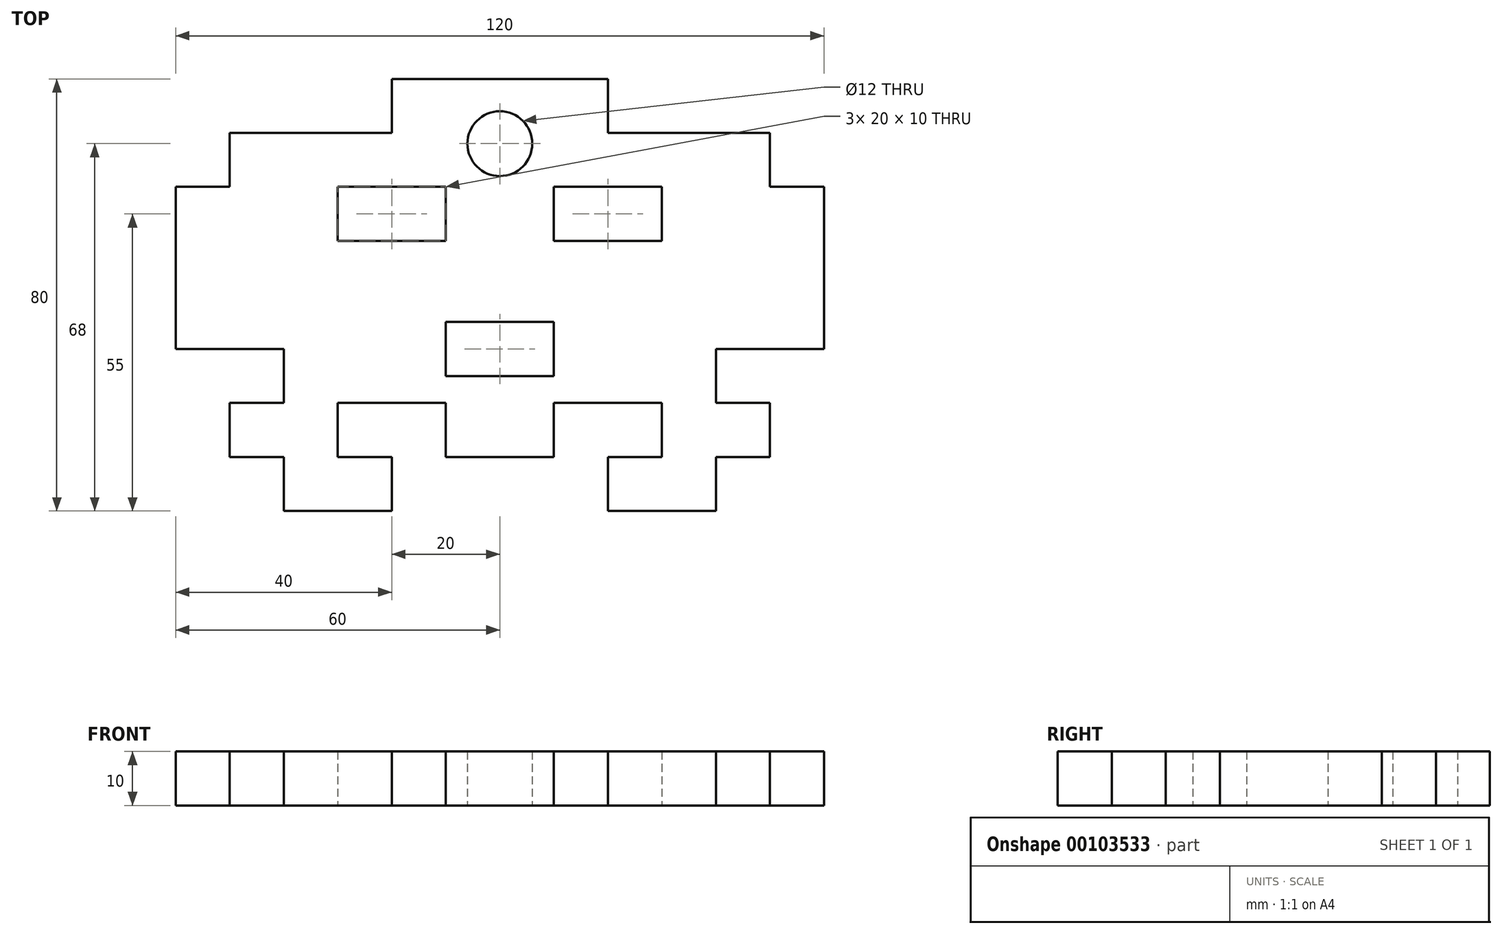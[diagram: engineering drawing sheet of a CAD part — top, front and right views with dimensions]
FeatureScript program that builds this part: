
annotation { "Feature Type Name" : "Feature", "Feature Type Description" : "" }
export const myFeature = defineFeature(function(context is Context, id is Id, definition is map)
    precondition{}
    {
        {
            var Q0;
            Q0=qCreatedBy(makeId("Top.planeOp"),FACE);
            var sketch = newSketch(context, id + "F0", { "sketchPlane" : qUnion([Q0]), "disableImprinting" : false});
            skLineSegment(sketch, "E0", {"start": v(0, 0) * mm, "end": v(-10, 0) * mm});
            skLineSegment(sketch, "E1", {"start": v(-10, 0) * mm, "end": v(-20, 0) * mm});
            skLineSegment(sketch, "E2", {"start": v(-20, 0) * mm, "end": v(-20, -10) * mm});
            skLineSegment(sketch, "E3", {"start": v(-20, -10) * mm, "end": v(-30, -10) * mm});
            skLineSegment(sketch, "E4", {"start": v(-30, -10) * mm, "end": v(-40, -10) * mm});
            skLineSegment(sketch, "E5", {"start": v(-40, -10) * mm, "end": v(-50, -10) * mm});
            skLineSegment(sketch, "E6", {"start": v(-50, -10) * mm, "end": v(-50, -20) * mm});
            skLineSegment(sketch, "E7", {"start": v(-50, -20) * mm, "end": v(-60, -20) * mm});
            skLineSegment(sketch, "E8", {"start": v(-60, -20) * mm, "end": v(-60, -30) * mm});
            skLineSegment(sketch, "E9", {"start": v(-60, -30) * mm, "end": v(-60, -40) * mm});
            skLineSegment(sketch, "E10", {"start": v(-60, -40) * mm, "end": v(-60, -50) * mm});
            skLineSegment(sketch, "E11", {"start": v(-60, -50) * mm, "end": v(-50, -50) * mm});
            skLineSegment(sketch, "E12", {"start": v(-50, -50) * mm, "end": v(-40, -50) * mm});
            skLineSegment(sketch, "E13", {"start": v(-40, -50) * mm, "end": v(-40, -60) * mm});
            skLineSegment(sketch, "E14", {"start": v(-40, -60) * mm, "end": v(-50, -60) * mm});
            skLineSegment(sketch, "E15", {"start": v(-50, -60) * mm, "end": v(-50, -70) * mm});
            skLineSegment(sketch, "E16", {"start": v(-50, -70) * mm, "end": v(-40, -70) * mm});
            skLineSegment(sketch, "E17", {"start": v(-40, -70) * mm, "end": v(-40, -80) * mm});
            skLineSegment(sketch, "E18", {"start": v(-40, -80) * mm, "end": v(-30, -80) * mm});
            skLineSegment(sketch, "E19", {"start": v(-30, -80) * mm, "end": v(-20, -80) * mm});
            skLineSegment(sketch, "E20", {"start": v(-20, -80) * mm, "end": v(-20, -70) * mm});
            skLineSegment(sketch, "E21", {"start": v(-20, -70) * mm, "end": v(-30, -70) * mm});
            skLineSegment(sketch, "E22", {"start": v(-30, -70) * mm, "end": v(-30, -60) * mm});
            skLineSegment(sketch, "E23", {"start": v(-30, -60) * mm, "end": v(-20, -60) * mm});
            skLineSegment(sketch, "E24", {"start": v(-20, -60) * mm, "end": v(-10, -60) * mm});
            skLineSegment(sketch, "E25", {"start": v(-10, -60) * mm, "end": v(-10, -70) * mm});
            skLineSegment(sketch, "E26", {"start": v(-10, -70) * mm, "end": v(0, -70) * mm});
            skLineSegment(sketch, "E27", {"start": v(0, -45) * mm, "end": v(-10, -45) * mm});
            skLineSegment(sketch, "E28", {"start": v(-10, -45) * mm, "end": v(-10, -55) * mm});
            skLineSegment(sketch, "E29", {"start": v(-10, -55) * mm, "end": v(0, -55) * mm});
            skLineSegment(sketch, "E30", {"start": v(-10, -60) * mm, "end": v(-10, -50) * mm, "construction": true});
            skLineSegment(sketch, "E31", {"start": v(-30, -20) * mm, "end": v(-20, -20) * mm});
            skLineSegment(sketch, "E32", {"start": v(-20, -20) * mm, "end": v(-10, -20) * mm});
            skLineSegment(sketch, "E33", {"start": v(-10, -20) * mm, "end": v(-10, -30) * mm});
            skLineSegment(sketch, "E34", {"start": v(-10, -30) * mm, "end": v(-20, -30) * mm});
            skLineSegment(sketch, "E35", {"start": v(-20, -30) * mm, "end": v(-30, -30) * mm});
            skLineSegment(sketch, "E36", {"start": v(-30, -30) * mm, "end": v(-30, -20) * mm});
            skLineSegment(sketch, "E37.MirrorCS", {"start": v(50, -60) * mm, "end": v(50, -70) * mm});
            skLineSegment(sketch, "E38.MirrorCS", {"start": v(30, -10) * mm, "end": v(40, -10) * mm});
            skLineSegment(sketch, "E39.MirrorCS", {"start": v(50, -20) * mm, "end": v(60, -20) * mm});
            skLineSegment(sketch, "E40.MirrorCS", {"start": v(20, -20) * mm, "end": v(10, -20) * mm});
            skLineSegment(sketch, "E41.MirrorCS", {"start": v(60, -40) * mm, "end": v(60, -50) * mm});
            skLineSegment(sketch, "E42.MirrorCS", {"start": v(10, 0) * mm, "end": v(20, 0) * mm});
            skLineSegment(sketch, "E43.MirrorCS", {"start": v(10, -20) * mm, "end": v(10, -30) * mm});
            skLineSegment(sketch, "E44.MirrorCS", {"start": v(40, -60) * mm, "end": v(50, -60) * mm});
            skLineSegment(sketch, "E45.MirrorCS", {"start": v(20, 0) * mm, "end": v(20, -10) * mm});
            skLineSegment(sketch, "E46.MirrorCS", {"start": v(0, 0) * mm, "end": v(10, 0) * mm});
            skLineSegment(sketch, "E47.MirrorCS", {"start": v(20, -10) * mm, "end": v(30, -10) * mm});
            skLineSegment(sketch, "E48.MirrorCS", {"start": v(10, -30) * mm, "end": v(20, -30) * mm});
            skLineSegment(sketch, "E49.MirrorCS", {"start": v(30, -30) * mm, "end": v(30, -20) * mm});
            skLineSegment(sketch, "E50.MirrorCS", {"start": v(30, -20) * mm, "end": v(20, -20) * mm});
            skLineSegment(sketch, "E51.MirrorCS", {"start": v(0, -45) * mm, "end": v(10, -45) * mm});
            skLineSegment(sketch, "E52.MirrorCS", {"start": v(50, -70) * mm, "end": v(40, -70) * mm});
            skLineSegment(sketch, "E53.MirrorCS", {"start": v(20, -80) * mm, "end": v(20, -70) * mm});
            skLineSegment(sketch, "E54.MirrorCS", {"start": v(20, -70) * mm, "end": v(30, -70) * mm});
            skLineSegment(sketch, "E55.MirrorCS", {"start": v(10, -55) * mm, "end": v(0, -55) * mm});
            skLineSegment(sketch, "E56.MirrorCS", {"start": v(60, -30) * mm, "end": v(60, -40) * mm});
            skLineSegment(sketch, "E57.MirrorCS", {"start": v(40, -80) * mm, "end": v(30, -80) * mm});
            skLineSegment(sketch, "E58.MirrorCS", {"start": v(60, -50) * mm, "end": v(50, -50) * mm});
            skLineSegment(sketch, "E59.MirrorCS", {"start": v(10, -60) * mm, "end": v(10, -70) * mm});
            skLineSegment(sketch, "E60.MirrorCS", {"start": v(30, -80) * mm, "end": v(20, -80) * mm});
            skLineSegment(sketch, "E61.MirrorCS", {"start": v(20, -30) * mm, "end": v(30, -30) * mm});
            skLineSegment(sketch, "E62.MirrorCS", {"start": v(40, -70) * mm, "end": v(40, -80) * mm});
            skLineSegment(sketch, "E63.MirrorCS", {"start": v(60, -20) * mm, "end": v(60, -30) * mm});
            skLineSegment(sketch, "E64.MirrorCS", {"start": v(50, -10) * mm, "end": v(50, -20) * mm});
            skLineSegment(sketch, "E65.MirrorCS", {"start": v(40, -50) * mm, "end": v(40, -60) * mm});
            skLineSegment(sketch, "E66.MirrorCS", {"start": v(30, -70) * mm, "end": v(30, -60) * mm});
            skLineSegment(sketch, "E67.MirrorCS", {"start": v(10, -45) * mm, "end": v(10, -55) * mm});
            skLineSegment(sketch, "E68.MirrorCS", {"start": v(10, -70) * mm, "end": v(0, -70) * mm});
            skLineSegment(sketch, "E69.MirrorCS", {"start": v(40, -10) * mm, "end": v(50, -10) * mm});
            skLineSegment(sketch, "E70.MirrorCS", {"start": v(30, -60) * mm, "end": v(20, -60) * mm});
            skLineSegment(sketch, "E71.MirrorCS", {"start": v(20, -60) * mm, "end": v(10, -60) * mm});
            skLineSegment(sketch, "E72.MirrorCS", {"start": v(50, -50) * mm, "end": v(40, -50) * mm});
            skCircle(sketch, "E73", {"center": v(0, -12) * mm, "radius": 6 * mm});
            skSolve(sketch);
        }
        {
            var Q0;
            Q0 = qSketchRegion(id + "F0", true);
            extrude(context, id + "F1", {"entities" : qUnion([Q0]), "depth" : 10 * mm});
        }
        {
            var Q0;
            Q0=qCreatedBy(makeId("Right.planeOp"),FACE);
            var sketch = newSketch(context, id + "F2", { "sketchPlane" : qUnion([Q0])});
            skLineSegment(sketch, "E74", {"start": v(-16, 0) * mm, "end": v(-16, 5) * mm});
            skLineSegment(sketch, "E75", {"start": v(-16, 5) * mm, "end": v(-7.11, 5) * mm});
            skLineSegment(sketch, "E76", {"start": v(-7.11, 5) * mm, "end": v(-10, 0) * mm});
            skLineSegment(sketch, "E77", {"start": v(-10, 0) * mm, "end": v(-16, 0) * mm});
            skSolve(sketch);
        }
        {
            var Q0;
            Q0 = qSketchRegion(id + "F2", true);
            extrude(context, id + "F3", {"entities" : qUnion([Q0]), "operationType" : NewBodyOperationType.REMOVE, "oppositeDirection" : true, "depth" : 6 * mm, "symmetric" : true});
        }
    });
